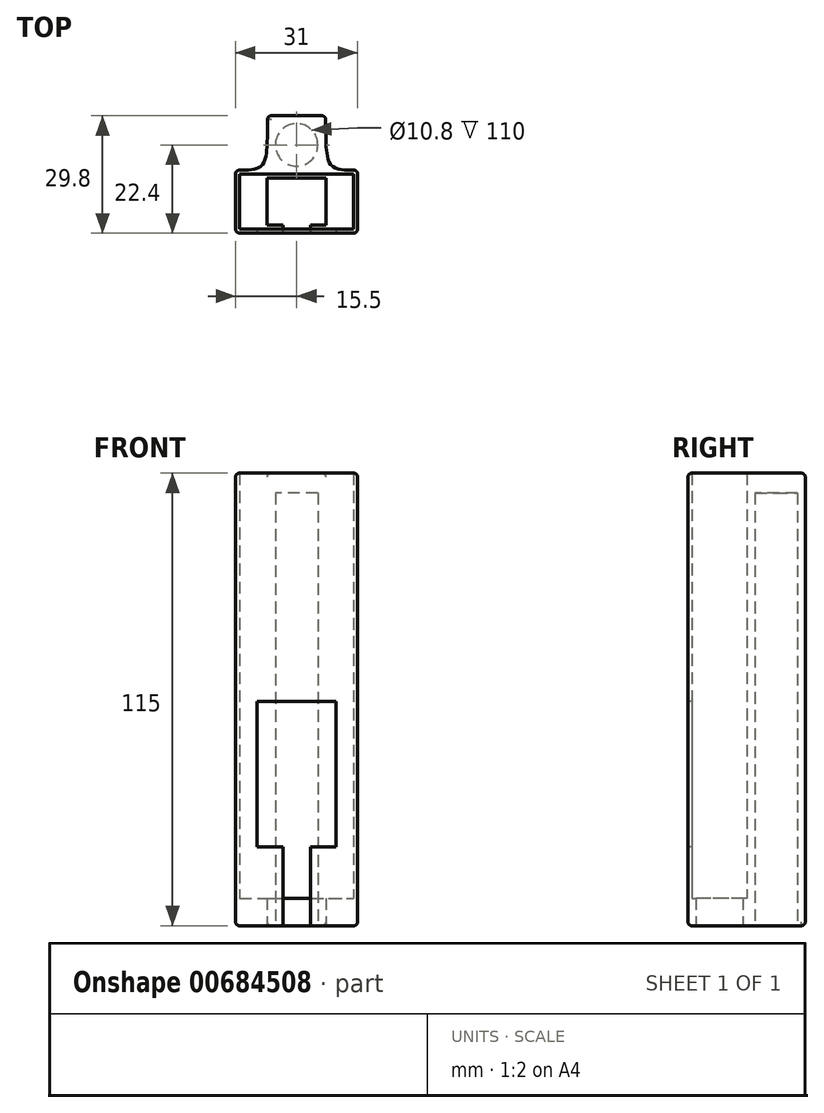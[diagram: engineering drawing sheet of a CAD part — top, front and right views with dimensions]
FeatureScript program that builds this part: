
annotation { "Feature Type Name" : "Feature", "Feature Type Description" : "" }
export const myFeature = defineFeature(function(context is Context, id is Id, definition is map)
    precondition{}
    {
        {
            var Q0;
            Q0=qCreatedBy(makeId("Top.planeOp"),FACE);
            var sketch = newSketch(context, id + "F0", { "sketchPlane" : qUnion([Q0])});
            skLineSegment(sketch, "E0.bottom", {"start": v(-7.5, 6) * mm, "end": v(7.5, 6) * mm});
            skLineSegment(sketch, "E0.top", {"start": v(-7.5, -6) * mm, "end": v(7.5, -6) * mm});
            skLineSegment(sketch, "E0.left", {"start": v(-7.5, 6) * mm, "end": v(-7.5, -6) * mm});
            skLineSegment(sketch, "E0.right", {"start": v(7.5, 6) * mm, "end": v(7.5, -6) * mm});
            skSolve(sketch);
        }
        {
            var Q0;
            Q0=makeQuery(id+"F0.imprint","IMPRINT",FACE,{"disambiguationData":[TD([[makeQuery(id+"F0.imprint","IMPRINT",EDGE,{"derivedFrom":sQuery(id+"F0.wireOp",EDGE,"3fn4VqtC-1CBd-aDJK-FRBe-rKAV0e28qjWR.bottom")}),-1.0]])]});
            var Q1;
            Q1=makeQuery(id+"F0.imprint","IMPRINT",FACE,{"disambiguationData":[TD([[makeQuery(id+"F0.imprint","IMPRINT",EDGE,{"derivedFrom":sQuery(id+"F0.wireOp",EDGE,"E0.bottom")}),-1.0]])]});
            extrude(context, id + "F1", {"entities" : qUnion([Q0, Q1]), "depth" : 7 * mm, "offsetDistance" : 25 * mm});
        }
        {
            var Q0;
            Q0=makeQuery(id+"F1.opExtrude","CAP_FACE",FACE,{"disambiguationData":[OSD([sQuery(id+"F0.wireOp",EDGE,"E0.bottom"),sQuery(id+"F0.wireOp",EDGE,"E0.top"),sQuery(id+"F0.wireOp",EDGE,"E0.left"),sQuery(id+"F0.wireOp",EDGE,"E0.right")])],"isStart":false});
            var sketch = newSketch(context, id + "F2", { "sketchPlane" : qUnion([Q0])});
            skLineSegment(sketch, "E1.bottom", {"start": v(-14.5, 7) * mm, "end": v(14.5, 7) * mm});
            skLineSegment(sketch, "E1.top", {"start": v(-14.5, -7) * mm, "end": v(14.5, -7) * mm});
            skLineSegment(sketch, "E1.left", {"start": v(-14.5, 7) * mm, "end": v(-14.5, -7) * mm});
            skLineSegment(sketch, "E1.right", {"start": v(14.5, 7) * mm, "end": v(14.5, -7) * mm});
            skSolve(sketch);
        }
        {
            var Q0;
            Q0=makeQuery(id+"F2.imprint","IMPRINT",FACE,{"disambiguationData":[TD([[makeQuery(id+"F2.imprint","IMPRINT",EDGE,{"derivedFrom":sQuery(id+"F2.wireOp",EDGE,"E1.bottom")}),-1.0]])]});
            var Q1;
            Q1=makeQuery(id+"F2.imprint","IMPRINT",FACE,{"disambiguationData":[TD([[makeQuery(id+"F2.imprint","IMPRINT",EDGE,{"derivedFrom":makeQuery(id+"F1.opExtrude","CAP_EDGE",EDGE,{"disambiguationData":[OSD([sQuery(id+"F0.wireOp",EDGE,"E0.bottom")])],"isStart":false})}),-1.0]])]});
            extrude(context, id + "F3", {"entities" : qUnion([Q0, Q1]), "operationType" : NewBodyOperationType.ADD, "depth" : 108 * mm, "offsetDistance" : 25 * mm});
        }
        {
            var Q0;
            Q0=qCreatedBy(makeId("Top.planeOp"),FACE);
            var sketch = newSketch(context, id + "F4", { "sketchPlane" : qUnion([Q0])});
            skLineSegment(sketch, "E2.bottom", {"start": v(15.5, -8) * mm, "end": v(-15.5, -8) * mm});
            skLineSegment(sketch, "E2.top", {"start": v(15.5, 8) * mm, "end": v(-15.5, 8) * mm});
            skLineSegment(sketch, "E2.left", {"start": v(15.5, -8) * mm, "end": v(15.5, 8) * mm});
            skLineSegment(sketch, "E2.right", {"start": v(-15.5, -8) * mm, "end": v(-15.5, 8) * mm});
            skCircle(sketch, "E3", {"center": v(0, 14.4) * mm, "radius": 5.4 * mm});
            skLineSegment(sketch, "E4.bottom", {"start": v(7.4, 8) * mm, "end": v(-7.4, 8) * mm});
            skLineSegment(sketch, "E4.top", {"start": v(7.4, 21.8) * mm, "end": v(-7.4, 21.8) * mm});
            skLineSegment(sketch, "E4.left", {"start": v(7.4, 8) * mm, "end": v(7.4, 21.8) * mm});
            skLineSegment(sketch, "E4.right", {"start": v(-7.4, 8) * mm, "end": v(-7.4, 21.8) * mm});
            skFitSpline(sketch, "E5", {"points": [v(7.4, 21.8) * mm, v(15.5, 8) * mm], "startDerivative": vector(0, -41.4) * mm, "endDerivative": vector(24.3, 0) * mm});
            skFitSpline(sketch, "E6", {"points": [v(-7.4, 21.8) * mm, v(-15.5, 8) * mm], "startDerivative": vector(0, -41.4) * mm, "endDerivative": vector(-24.3, 0) * mm});
            skSolve(sketch);
        }
        {
            var Q0;
            Q0=makeQuery(id+"F4.imprint","IMPRINT",FACE,{"disambiguationData":[TD([[makeQuery(id+"F4.imprint","IMPRINT",EDGE,{"derivedFrom":sQuery(id+"F4.wireOp",EDGE,"E2.bottom")}),-1.0]])]});
            var Q1;
            Q1=makeQuery(id+"F4.imprint","IMPRINT",FACE,{"disambiguationData":[TD([[makeQuery(id+"F4.imprint","IMPRINT",EDGE,{"derivedFrom":sQuery(id+"F4.wireOp",EDGE,"E3")}),-1.0]])]});
            var Q2;
            Q2=makeQuery(id+"F4.imprint","IMPRINT",FACE,{"disambiguationData":[TD([[makeQuery(id+"F4.imprint","IMPRINT",EDGE,{"derivedFrom":sQuery(id+"F4.wireOp",EDGE,"E3")}),1.0]])]});
            var Q3;
            {var subQ2=sQuery(id+"F4.wireOp",EDGE,"E4.right");Q3=makeQuery(id+"F4.imprint","IMPRINT",FACE,{"disambiguationData":[TD([[makeQuery(id+"F4.imprint","IMPRINT",EDGE,{"derivedFrom":subQ2}),1.0]])]});}
            var Q4;
            {var subQ2=sQuery(id+"F4.wireOp",EDGE,"E4.left");Q4=makeQuery(id+"F4.imprint","IMPRINT",FACE,{"disambiguationData":[TD([[makeQuery(id+"F4.imprint","IMPRINT",EDGE,{"derivedFrom":subQ2}),-1.0]])]});}
            extrude(context, id + "F5", {"entities" : qUnion([Q0, Q1, Q2, Q3, Q4]), "depth" : 115 * mm, "offsetDistance" : 25 * mm});
        }
        {
            var Q0;
            Q0=makeQuery(id+"F1.opExtrude","SWEPT_BODY",BODY,{"disambiguationData":[OSD([sQuery(id+"F0.wireOp",EDGE,"E0.bottom"),sQuery(id+"F0.wireOp",EDGE,"E0.top"),sQuery(id+"F0.wireOp",EDGE,"E0.left"),sQuery(id+"F0.wireOp",EDGE,"E0.right")])]});
            var Q1;
            Q1=makeQuery(id+"F5.opExtrude","SWEPT_BODY",BODY,{"disambiguationData":[OSD([sQuery(id+"F4.wireOp",EDGE,"E2.bottom"),sQuery(id+"F4.wireOp",EDGE,"E2.top"),sQuery(id+"F4.wireOp",EDGE,"E2.left"),sQuery(id+"F4.wireOp",EDGE,"E2.right")])]});
            booleanBodies(context, id + "F6", {"operationType" : BooleanOperationType.SUBTRACTION, "tools" : qUnion([Q0]), "targets" : qUnion([Q1])});
        }
        {
            var Q0;
            Q0=makeQuery(id+"F4.imprint","IMPRINT",FACE,{"disambiguationData":[TD([[makeQuery(id+"F4.imprint","IMPRINT",EDGE,{"derivedFrom":sQuery(id+"F4.wireOp",EDGE,"E3")}),1.0]])]});
            extrude(context, id + "F7", {"entities" : qUnion([Q0]), "operationType" : NewBodyOperationType.REMOVE, "depth" : 110 * mm, "offsetDistance" : 25 * mm});
        }
        {
            var Q0;
            Q0=makeQuery(id+"F5.opExtrude","SWEPT_FACE",FACE,{"disambiguationData":[OSD([sQuery(id+"F4.wireOp",EDGE,"E2.bottom")])]});
            var sketch = newSketch(context, id + "F8", { "sketchPlane" : qUnion([Q0])});
            skLineSegment(sketch, "E7.bottom", {"start": v(-3.5, 0) * mm, "end": v(3.5, 0) * mm});
            skLineSegment(sketch, "E7.top", {"start": v(-3.5, 20) * mm, "end": v(3.5, 20) * mm});
            skLineSegment(sketch, "E7.left", {"start": v(-3.5, 0) * mm, "end": v(-3.5, 20) * mm});
            skLineSegment(sketch, "E7.right", {"start": v(3.5, 0) * mm, "end": v(3.5, 20) * mm});
            skLineSegment(sketch, "E8.bottom", {"start": v(10, 20) * mm, "end": v(-10, 20) * mm});
            skLineSegment(sketch, "E8.top", {"start": v(10, 57) * mm, "end": v(-10, 57) * mm});
            skLineSegment(sketch, "E8.left", {"start": v(10, 20) * mm, "end": v(10, 57) * mm});
            skLineSegment(sketch, "E8.right", {"start": v(-10, 20) * mm, "end": v(-10, 57) * mm});
            skSolve(sketch);
        }
        {
            var Q0;
            Q0=makeQuery(id+"F8.imprint","IMPRINT",FACE,{"disambiguationData":[TD([[makeQuery(id+"F8.imprint","IMPRINT",EDGE,{"derivedFrom":sQuery(id+"F8.wireOp",EDGE,"E8.top")}),1.0]])]});
            var Q1;
            Q1=makeQuery(id+"F8.imprint","IMPRINT",FACE,{"disambiguationData":[TD([[makeQuery(id+"F8.imprint","IMPRINT",EDGE,{"derivedFrom":sQuery(id+"F8.wireOp",EDGE,"E7.bottom")}),-1.0]])]});
            extrude(context, id + "F9", {"entities" : qUnion([Q0, Q1]), "operationType" : NewBodyOperationType.REMOVE, "oppositeDirection" : true, "depth" : 5 * mm, "offsetDistance" : 25 * mm});
        }
        {
            var Q0;
            Q0=makeQuery(id+"F5.opExtrude","SWEPT_EDGE",EDGE,{"disambiguationData":[OSD([sQuery(id+"F4.wireOp",EDGE,"E4.top"),sQuery(id+"F4.wireOp",EDGE,"E4.right")])]});
            var Q1;
            Q1=makeQuery(id+"F5.opExtrude","SWEPT_EDGE",EDGE,{"disambiguationData":[OSD([sQuery(id+"F4.wireOp",EDGE,"E4.top"),sQuery(id+"F4.wireOp",EDGE,"E4.left")])]});
            var Q2;
            Q2=makeQuery(id+"F5.opExtrude","CAP_EDGE",EDGE,{"disambiguationData":[OSD([sQuery(id+"F4.wireOp",EDGE,"E4.right")])],"isStart":false});
            var Q3;
            Q3=makeQuery(id+"F5.opExtrude","CAP_EDGE",EDGE,{"disambiguationData":[OSD([sQuery(id+"F4.wireOp",EDGE,"E4.top")])],"isStart":false});
            var Q4;
            Q4=makeQuery(id+"F5.opExtrude","CAP_EDGE",EDGE,{"disambiguationData":[OSD([sQuery(id+"F4.wireOp",EDGE,"E4.left")])],"isStart":false});
            var Q5;
            Q5=makeQuery(id+"F5.opExtrude","CAP_EDGE",EDGE,{"disambiguationData":[OSD([sQuery(id+"F4.wireOp",EDGE,"E4.right")])],"isStart":true});
            var Q6;
            Q6=makeQuery(id+"F5.opExtrude","CAP_EDGE",EDGE,{"disambiguationData":[OSD([sQuery(id+"F4.wireOp",EDGE,"E4.top")])],"isStart":true});
            var Q7;
            Q7=makeQuery(id+"F5.opExtrude","CAP_EDGE",EDGE,{"disambiguationData":[OSD([sQuery(id+"F4.wireOp",EDGE,"E4.left")])],"isStart":true});
            var Q8;
            {var subQ0=sQuery(id+"F4.wireOp",EDGE,"E2.top");Q8=makeQuery(id+"F5.opExtrude","CAP_EDGE",EDGE,{"disambiguationData":[OSD([subQ0]),TDD([makeQuery(id+"F4.imprint","IMPRINT",EDGE,{"disambiguationData":[TD([[makeQuery(id+"F4.imprint","INTERSECT",VERTEX,{"derivedFrom":[subQ0,sQuery(id+"F4.wireOp",EDGE,"E2.left")]}),-1.0]])],"derivedFrom":subQ0})])],"isStart":true});}
            var Q9;
            {var subQ0=sQuery(id+"F4.wireOp",EDGE,"E2.top");Q9=makeQuery(id+"F5.opExtrude","CAP_EDGE",EDGE,{"disambiguationData":[OSD([subQ0]),TDD([makeQuery(id+"F4.imprint","IMPRINT",EDGE,{"disambiguationData":[TD([[makeQuery(id+"F4.imprint","INTERSECT",VERTEX,{"derivedFrom":[subQ0,sQuery(id+"F4.wireOp",EDGE,"E2.right")]}),1.0]])],"derivedFrom":subQ0})])],"isStart":true});}
            var Q10;
            Q10=makeQuery(id+"F5.opExtrude","SWEPT_EDGE",EDGE,{"disambiguationData":[OSD([sQuery(id+"F4.wireOp",EDGE,"E2.top"),sQuery(id+"F4.wireOp",EDGE,"E2.right")])]});
            var Q11;
            Q11=makeQuery(id+"F5.opExtrude","CAP_EDGE",EDGE,{"disambiguationData":[OSD([sQuery(id+"F4.wireOp",EDGE,"E2.right")])],"isStart":true});
            var Q12;
            Q12=makeQuery(id+"F5.opExtrude","SWEPT_EDGE",EDGE,{"disambiguationData":[OSD([sQuery(id+"F4.wireOp",EDGE,"E2.bottom"),sQuery(id+"F4.wireOp",EDGE,"E2.right")])]});
            var Q13;
            Q13=makeQuery(id+"F5.opExtrude","CAP_EDGE",EDGE,{"disambiguationData":[OSD([sQuery(id+"F4.wireOp",EDGE,"E2.bottom")])],"isStart":true});
            var Q14;
            Q14=makeQuery(id+"F5.opExtrude","CAP_EDGE",EDGE,{"disambiguationData":[OSD([sQuery(id+"F4.wireOp",EDGE,"E2.bottom")])],"isStart":false});
            var Q15;
            {var subQ0=sQuery(id+"F4.wireOp",EDGE,"E2.top");Q15=makeQuery(id+"F5.opExtrude","CAP_EDGE",EDGE,{"disambiguationData":[OSD([subQ0]),TDD([makeQuery(id+"F4.imprint","IMPRINT",EDGE,{"disambiguationData":[TD([[makeQuery(id+"F4.imprint","INTERSECT",VERTEX,{"derivedFrom":[subQ0,sQuery(id+"F4.wireOp",EDGE,"E2.right")]}),1.0]])],"derivedFrom":subQ0})])],"isStart":false});}
            var Q16;
            {var subQ0=sQuery(id+"F4.wireOp",EDGE,"E2.top");Q16=makeQuery(id+"F5.opExtrude","CAP_EDGE",EDGE,{"disambiguationData":[OSD([subQ0]),TDD([makeQuery(id+"F4.imprint","IMPRINT",EDGE,{"disambiguationData":[TD([[makeQuery(id+"F4.imprint","INTERSECT",VERTEX,{"derivedFrom":[subQ0,sQuery(id+"F4.wireOp",EDGE,"E2.left")]}),-1.0]])],"derivedFrom":subQ0})])],"isStart":false});}
            var Q17;
            Q17=makeQuery(id+"F5.opExtrude","CAP_EDGE",EDGE,{"disambiguationData":[OSD([sQuery(id+"F4.wireOp",EDGE,"E2.left")])],"isStart":false});
            var Q18;
            Q18=makeQuery(id+"F5.opExtrude","SWEPT_EDGE",EDGE,{"disambiguationData":[OSD([sQuery(id+"F4.wireOp",EDGE,"E2.top"),sQuery(id+"F4.wireOp",EDGE,"E2.left")])]});
            var Q19;
            Q19=makeQuery(id+"F5.opExtrude","SWEPT_EDGE",EDGE,{"disambiguationData":[OSD([sQuery(id+"F4.wireOp",EDGE,"E2.bottom"),sQuery(id+"F4.wireOp",EDGE,"E2.left")])]});
            var Q20;
            Q20=makeQuery(id+"F5.opExtrude","CAP_EDGE",EDGE,{"disambiguationData":[OSD([sQuery(id+"F4.wireOp",EDGE,"E2.right")])],"isStart":false});
            var Q21;
            Q21=makeQuery(id+"F5.opExtrude","CAP_EDGE",EDGE,{"disambiguationData":[OSD([sQuery(id+"F4.wireOp",EDGE,"E2.left")])],"isStart":true});
            var Q22;
            Q22=makeQuery(id+"F7.boolean.opBoolean","COPY",EDGE,{"derivedFrom":makeQuery(id+"F7.opExtrude","CAP_EDGE",EDGE,{"disambiguationData":[OSD([sQuery(id+"F4.wireOp",EDGE,"E3")])],"isStart":true})});
            var Q23;
            Q23=makeQuery(id+"F5.opExtrude","CAP_EDGE",EDGE,{"disambiguationData":[OSD([sQuery(id+"F4.wireOp",EDGE,"E5")])],"isStart":true});
            var Q24;
            Q24=makeQuery(id+"F5.opExtrude","CAP_EDGE",EDGE,{"disambiguationData":[OSD([sQuery(id+"F4.wireOp",EDGE,"E6")])],"isStart":true});
            var Q25;
            Q25=makeQuery(id+"F5.opExtrude","CAP_EDGE",EDGE,{"disambiguationData":[OSD([sQuery(id+"F4.wireOp",EDGE,"E5")])],"isStart":false});
            var Q26;
            Q26=makeQuery(id+"F5.opExtrude","CAP_EDGE",EDGE,{"disambiguationData":[OSD([sQuery(id+"F4.wireOp",EDGE,"E6")])],"isStart":false});
            var Q27;
            Q27=makeQuery(id+"F9.boolean.opBoolean","COPY",EDGE,{"derivedFrom":makeQuery(id+"F9.opExtrude","CAP_EDGE",EDGE,{"disambiguationData":[OSD([sQuery(id+"F8.wireOp",EDGE,"E7.left")])],"isStart":true})});
            var Q28;
            Q28=makeQuery(id+"F9.boolean.opBoolean","COPY",EDGE,{"derivedFrom":makeQuery(id+"F9.opExtrude","CAP_EDGE",EDGE,{"disambiguationData":[OSD([sQuery(id+"F8.wireOp",EDGE,"E8.right")])],"isStart":true})});
            var Q29;
            {var subQ0=sQuery(id+"F8.wireOp",EDGE,"E8.bottom");Q29=makeQuery(id+"F9.boolean.opBoolean","COPY",EDGE,{"derivedFrom":makeQuery(id+"F9.opExtrude","CAP_EDGE",EDGE,{"disambiguationData":[OSD([subQ0]),TDD([makeQuery(id+"F8.imprint","IMPRINT",EDGE,{"disambiguationData":[TD([[makeQuery(id+"F8.imprint","INTERSECT",VERTEX,{"derivedFrom":[sQuery(id+"F8.wireOp",EDGE,"E7.left"),subQ0]}),-1.0]])],"derivedFrom":subQ0})])],"isStart":true})});}
            var Q30;
            Q30=makeQuery(id+"F9.boolean.opBoolean","COPY",EDGE,{"derivedFrom":makeQuery(id+"F9.opExtrude","CAP_EDGE",EDGE,{"disambiguationData":[OSD([sQuery(id+"F8.wireOp",EDGE,"E8.top")])],"isStart":true})});
            var Q31;
            Q31=makeQuery(id+"F9.boolean.opBoolean","COPY",EDGE,{"derivedFrom":makeQuery(id+"F9.opExtrude","CAP_EDGE",EDGE,{"disambiguationData":[OSD([sQuery(id+"F8.wireOp",EDGE,"E8.left")])],"isStart":true})});
            var Q32;
            {var subQ0=sQuery(id+"F8.wireOp",EDGE,"E8.bottom");Q32=makeQuery(id+"F9.boolean.opBoolean","COPY",EDGE,{"derivedFrom":makeQuery(id+"F9.opExtrude","CAP_EDGE",EDGE,{"disambiguationData":[OSD([subQ0]),TDD([makeQuery(id+"F8.imprint","IMPRINT",EDGE,{"disambiguationData":[TD([[makeQuery(id+"F8.imprint","INTERSECT",VERTEX,{"derivedFrom":[sQuery(id+"F8.wireOp",EDGE,"E7.right"),subQ0]}),1.0]])],"derivedFrom":subQ0})])],"isStart":true})});}
            var Q33;
            Q33=makeQuery(id+"F9.boolean.opBoolean","COPY",EDGE,{"derivedFrom":makeQuery(id+"F9.opExtrude","CAP_EDGE",EDGE,{"disambiguationData":[OSD([sQuery(id+"F8.wireOp",EDGE,"E7.right")])],"isStart":true})});
            fillet(context, id + "F10", {"entities" : qUnion([Q0, Q1, Q2, Q3, Q4, Q5, Q6, Q7, Q8, Q9, Q10, Q11, Q12, Q13, Q14, Q15, Q16, Q17, Q18, Q19, Q20, Q21, Q22, Q23, Q24, Q25, Q26, Q27, Q28, Q29, Q30, Q31, Q32, Q33]), "radius" : 1 * mm, "allowEdgeOverflow" : false});
        }
    });
